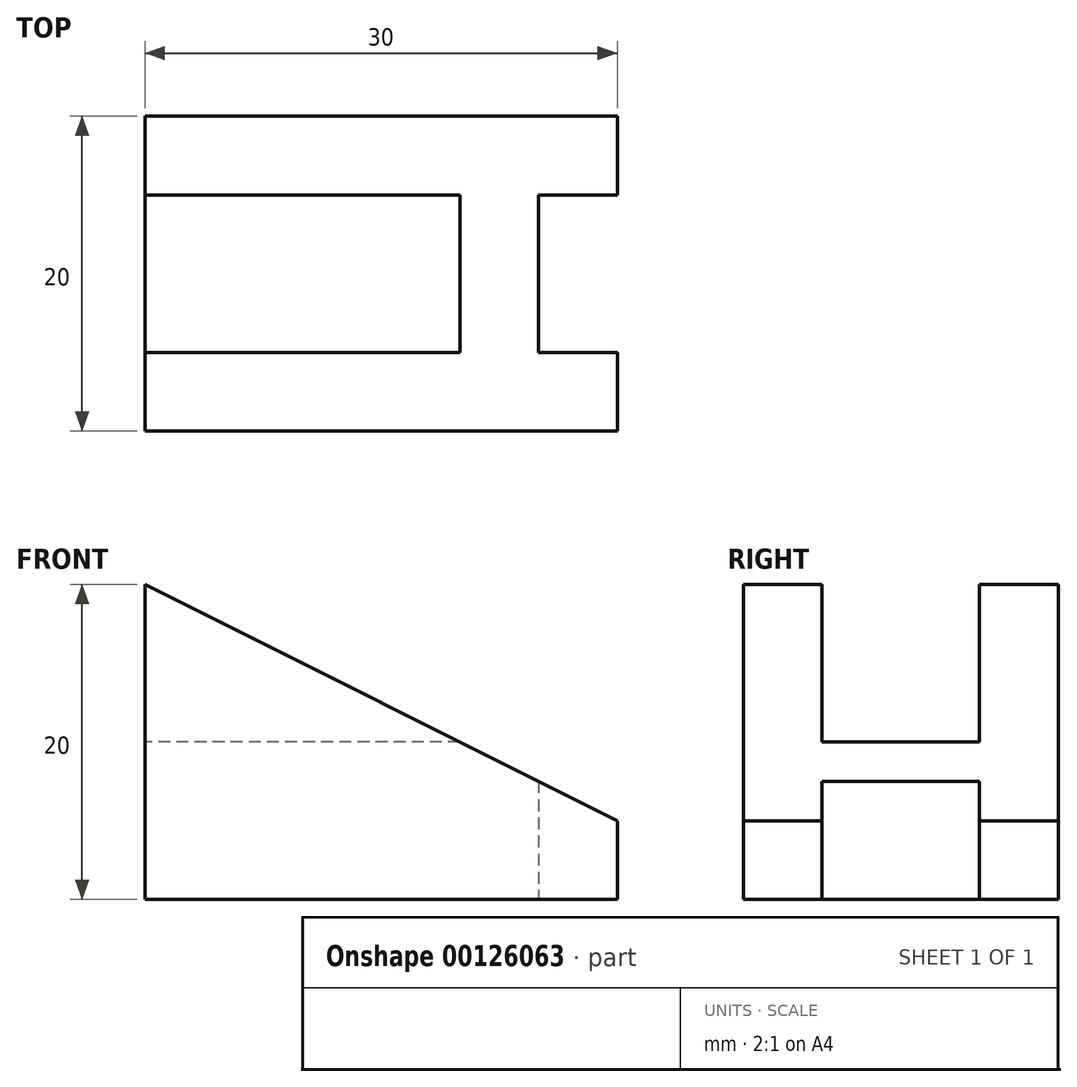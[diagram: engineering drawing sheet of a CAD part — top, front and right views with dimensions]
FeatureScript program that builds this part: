
annotation { "Feature Type Name" : "Feature", "Feature Type Description" : "" }
export const myFeature = defineFeature(function(context is Context, id is Id, definition is map)
    precondition{}
    {
        {
            var Q0;
            Q0=qCreatedBy(makeId("Front.planeOp"),FACE);
            var sketch = newSketch(context, id + "F0", { "sketchPlane" : qUnion([Q0])});
            skLineSegment(sketch, "E0", {"start": v(0, 0) * mm, "end": v(30, 0) * mm});
            skLineSegment(sketch, "E1", {"start": v(30, 0) * mm, "end": v(30, 5) * mm});
            skLineSegment(sketch, "E2", {"start": v(30, 5) * mm, "end": v(0, 20) * mm});
            skLineSegment(sketch, "E3", {"start": v(0, 20) * mm, "end": v(0, 0) * mm});
            skSolve(sketch);
        }
        {
            var Q0;
            Q0=makeQuery(id+"F0.imprint","IMPRINT",FACE,{"disambiguationData":[TD([[makeQuery(id+"F0.imprint","IMPRINT",EDGE,{"derivedFrom":sQuery(id+"F0.wireOp",EDGE,"E0")}),1.0]])]});
            extrude(context, id + "F1", {"entities" : qUnion([Q0]), "endBound" : BoundingType.SYMMETRIC, "depth" : 20 * mm});
        }
        {
            var Q0;
            Q0=makeQuery(id+"F1.opExtrude","SWEPT_FACE",FACE,{"disambiguationData":[OSD([sQuery(id+"F0.wireOp",EDGE,"E3")])]});
            var sketch = newSketch(context, id + "F2", { "sketchPlane" : qUnion([Q0])});
            skLineSegment(sketch, "E4", {"start": v(-5, 20) * mm, "end": v(-5, 10) * mm});
            skLineSegment(sketch, "E5", {"start": v(-5, 10) * mm, "end": v(5, 10) * mm});
            skLineSegment(sketch, "E6", {"start": v(5, 10) * mm, "end": v(5, 20) * mm});
            skLineSegment(sketch, "E7", {"start": v(-5, 20) * mm, "end": v(5, 20) * mm});
            skSolve(sketch);
        }
        {
            var Q0;
            Q0=makeQuery(id+"F2.imprint","IMPRINT",FACE,{"disambiguationData":[TD([[makeQuery(id+"F2.imprint","IMPRINT",EDGE,{"derivedFrom":sQuery(id+"F2.wireOp",EDGE,"E4")}),1.0]])]});
            extrude(context, id + "F3", {"entities" : qUnion([Q0]), "operationType" : NewBodyOperationType.REMOVE, "oppositeDirection" : true, "depth" : 20 * mm});
        }
        {
            var Q0;
            Q0=makeQuery(id+"F1.opExtrude","SWEPT_FACE",FACE,{"disambiguationData":[OSD([sQuery(id+"F0.wireOp",EDGE,"E0")])]});
            var sketch = newSketch(context, id + "F4", { "sketchPlane" : qUnion([Q0])});
            skLineSegment(sketch, "E8", {"start": v(30, 5) * mm, "end": v(25, 5) * mm});
            skLineSegment(sketch, "E9", {"start": v(25, 5) * mm, "end": v(25, -5) * mm});
            skLineSegment(sketch, "E10", {"start": v(25, -5) * mm, "end": v(30, -5) * mm});
            skLineSegment(sketch, "E11", {"start": v(30, -5) * mm, "end": v(30, 5) * mm});
            skSolve(sketch);
        }
        {
            var Q0;
            Q0=makeQuery(id+"F4.imprint","IMPRINT",FACE,{"disambiguationData":[TD([[makeQuery(id+"F4.imprint","IMPRINT",EDGE,{"derivedFrom":sQuery(id+"F4.wireOp",EDGE,"E8")}),1.0]])]});
            extrude(context, id + "F5", {"entities" : qUnion([Q0]), "operationType" : NewBodyOperationType.REMOVE, "oppositeDirection" : true, "depth" : 25 * mm});
        }
    });
